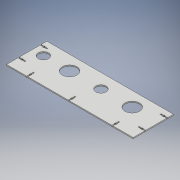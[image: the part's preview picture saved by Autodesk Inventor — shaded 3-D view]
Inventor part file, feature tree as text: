
AUTODESK INVENTOR PART (.ipt)
format: ipt  version: 2018 (Build 220112000, 112)  size: 256,000 bytes
history: native  units: mm
features: extrude x4, sketch x4, plane x1, mirror x1, projected_geometry x1
ambient origin geometry x8: Origin, YZ Plane, XZ Plane, XY Plane, X Axis, Y Axis, Z Axis, Center Point
bodies: Body1 (feature_tree)
feature tree (11):
  extrude  "Extrusion2"  Depth=140.0mm
  extrude  "Extrusion3"  Depth=4.0mm
  extrude  "Extrusion4"  Depth=51.0mm
  plane  "Work Plane1"
  mirror  "Mirror1"
  extrude  "Extrusion5"  Depth=10.0mm
  sketch  "Sketch2"  dims[d8=440.0mm d9=140.0mm]
  sketch  "Sketch3"  dims[d11=4.0mm d12=0.0mm d13=91.0mm]
  projected_geometry  "Projected Loop1"
  sketch  "Sketch4"  dims[d14=36.0mm d15=51.0mm]
  sketch  "Sketch5"  dims[d16=38.0mm d17=109.0mm d18=36.0mm d19=109.0mm d20=51.0mm d21=4.0mm d22=0.0mm d23=50.0mm d24=4.0mm d25=27.0mm d26=3.6mm d27=3.0mm d28=6.0mm d29=10.0mm d30=140.0mm d31=20.0mm d32=27.0mm d33=3.0mm d34=6.0mm d35=40.0mm d36=3.6mm d37=4.0mm d38=0.0mm d39=70.0mm d40=3.6mm d41=3.6mm d42=6.0mm d43=1.2mm d44=3.0mm d45=1.2mm d46=3.6mm d47=3.6mm d48=6.0mm d49=1.2mm d50=3.0mm d51=1.2mm d52=3.6mm d53=3.6mm d54=6.0mm d55=1.2mm d56=3.0mm d57=1.2mm d58=70.0mm d59=440.0mm d60=221.8mm d61=10.0mm d62=0.0mm]
